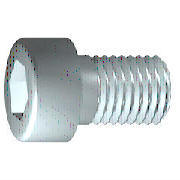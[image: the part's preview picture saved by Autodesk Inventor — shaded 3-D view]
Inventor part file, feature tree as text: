
AUTODESK INVENTOR PART (.ipt)
format: ipt  version: 2020 (Build 240168000, 168)  size: 188,416 bytes
history: native  units: mm (DEFAULTED — no unit token found)
features: sketch x2, other x1, extrude x1, plane x1, fillet x1
ambient origin geometry x7: Origin, YZ Plane, XY Plane, X Axis, Y Axis, Z Axis, Center Point
bodies: Solid1 (feature_tree)
feature tree (6):
  other  "Bryła"
  extrude  "Szczelina"  Depth=24.0mm
  plane  "Work Plane1"
  fillet  "Fillet2"  Radius=0.61355mm
  sketch  "Szkic1"
  sketch  "Szkic2"
